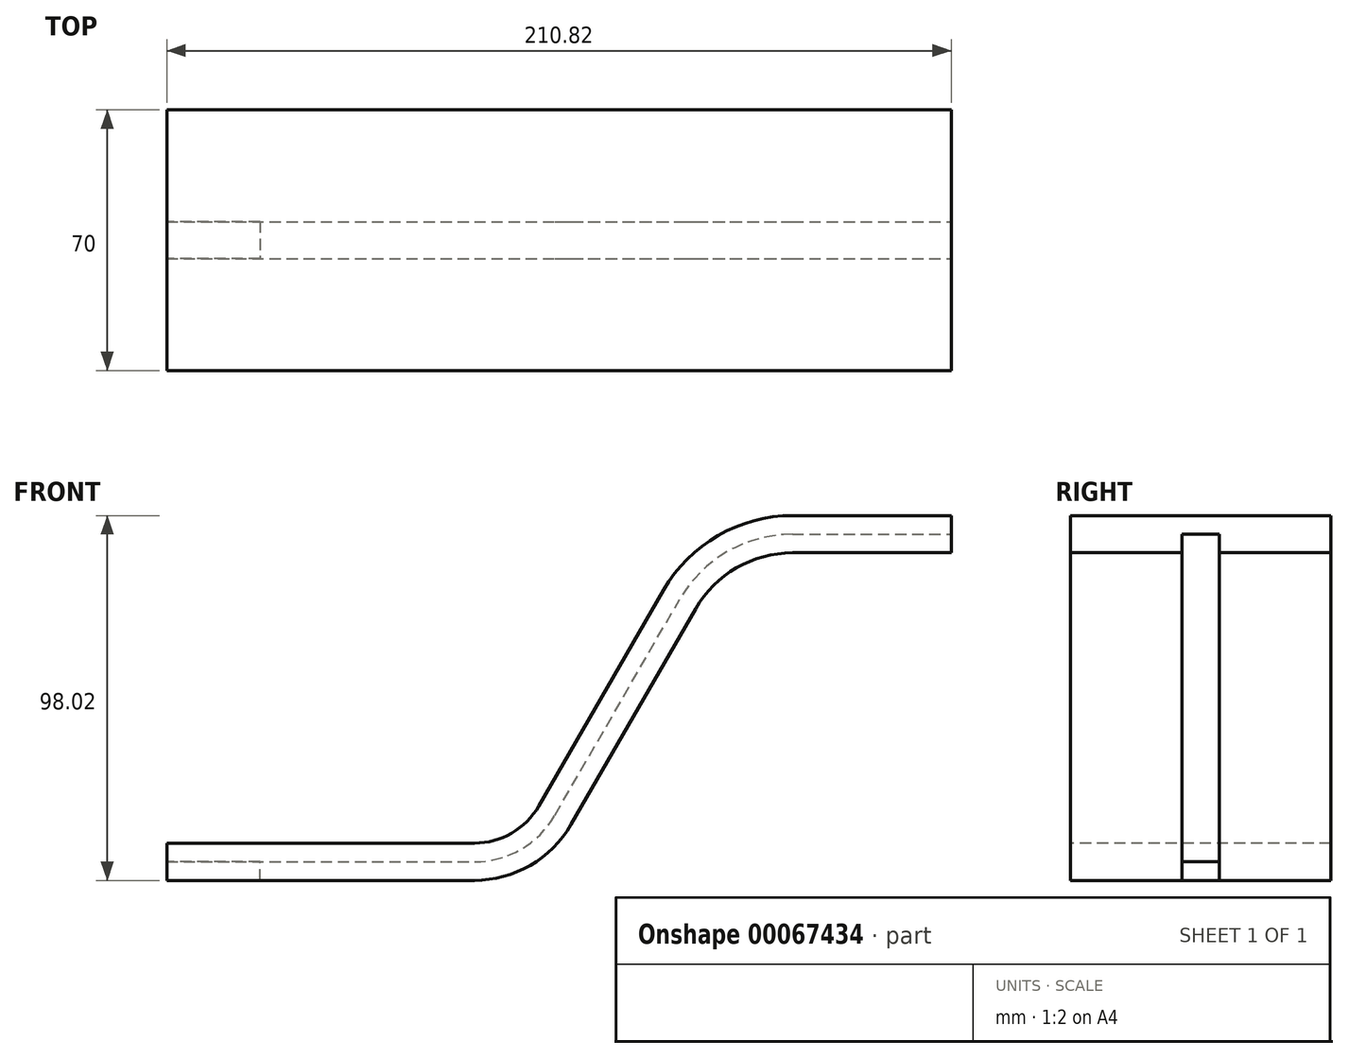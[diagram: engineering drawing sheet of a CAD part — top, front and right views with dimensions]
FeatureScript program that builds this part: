
annotation { "Feature Type Name" : "Feature", "Feature Type Description" : "" }
export const myFeature = defineFeature(function(context is Context, id is Id, definition is map)
    precondition{}
    {
        {
            var Q0;
            Q0=qCreatedBy(makeId("Front.planeOp"),FACE);
            var sketch = newSketch(context, id + "F0", { "sketchPlane" : qUnion([Q0])});
            skLineSegment(sketch, "E0", {"start": v(0, 0) * mm, "end": v(82.68, 0) * mm});
            skLineSegment(sketch, "E1", {"start": v(108.66, 15) * mm, "end": v(142.16, 73.02) * mm});
            skLineSegment(sketch, "E2", {"start": v(168.14, 88.02) * mm, "end": v(210.82, 88.02) * mm});
            skPoint(sketch, "E3.visualSharp", {"position": v(150.82, 88.02) * mm});
            skArc(sketch, "E3.filletArc", {"start": v(168.14, 88.02) * mm, "mid": v(153.14, 84) * mm, "end": v(142.16, 73.02) * mm});
            skPoint(sketch, "E4.visualSharp", {"position": v(100, 0) * mm});
            skArc(sketch, "E4.filletArc", {"start": v(82.68, 0) * mm, "mid": v(97.68, 4.02) * mm, "end": v(108.66, 15) * mm});
            skSolve(sketch);
        }
        {
            var Q0;
            Q0=qCreatedBy(makeId("Right.planeOp"),FACE);
            var sketch = newSketch(context, id + "F1", { "sketchPlane" : qUnion([Q0])});
            skLineSegment(sketch, "E5.bottom", {"start": v(35, 0) * mm, "end": v(5, 0) * mm});
            skLineSegment(sketch, "E5.top", {"start": v(35, 10) * mm, "end": v(-35, 10) * mm});
            skLineSegment(sketch, "E5.left", {"start": v(35, 0) * mm, "end": v(35, 10) * mm});
            skLineSegment(sketch, "E5.right", {"start": v(-35, 0) * mm, "end": v(-35, 10) * mm});
            skLineSegment(sketch, "E6.top", {"start": v(5, 5) * mm, "end": v(-5, 5) * mm});
            skLineSegment(sketch, "E6.left", {"start": v(5, 0) * mm, "end": v(5, 5) * mm});
            skLineSegment(sketch, "E6.right", {"start": v(-5, 0) * mm, "end": v(-5, 5) * mm});
            skLineSegment(sketch, "E7.trimOffspring", {"start": v(-5, 0) * mm, "end": v(-35, 0) * mm});
            skSolve(sketch);
        }
        {
            var Q0;
            Q0=makeQuery(id+"F1.imprint","IMPRINT",FACE,{"disambiguationData":[TD([[makeQuery(id+"F1.imprint","IMPRINT",EDGE,{"derivedFrom":sQuery(id+"F1.wireOp",EDGE,"E5.bottom")}),-1.0]])]});
            var Q1;
            Q1=sQuery(id+"F0.wireOp",EDGE,"E0");
            var Q2;
            Q2=sQuery(id+"F0.wireOp",EDGE,"E4.filletArc");
            var Q3;
            Q3=sQuery(id+"F0.wireOp",EDGE,"E1");
            var Q4;
            Q4=sQuery(id+"F0.wireOp",EDGE,"E3.filletArc");
            var Q5;
            Q5=sQuery(id+"F0.wireOp",EDGE,"E2");
            sweep(context, id + "F2", {"profiles" : qUnion([Q0]), "path" : qUnion([Q1, Q2, Q3, Q4, Q5])});
        }
        {
            var Q0;
            Q0=makeQuery(id+"F2.opSweep","CAP_FACE",FACE,{"disambiguationData":[OSD([sQuery(id+"F0.wireOp",VERTEX,"E0.start"),sQuery(id+"F1.wireOp",EDGE,"E5.bottom"),sQuery(id+"F1.wireOp",EDGE,"E5.top"),sQuery(id+"F1.wireOp",EDGE,"E5.left"),sQuery(id+"F1.wireOp",EDGE,"E5.right"),sQuery(id+"F1.wireOp",EDGE,"E6.top"),sQuery(id+"F1.wireOp",EDGE,"E6.left"),sQuery(id+"F1.wireOp",EDGE,"E6.right"),sQuery(id+"F1.wireOp",EDGE,"E7.trimOffspring")])],"isStart":true});
            var sketch = newSketch(context, id + "F3", { "sketchPlane" : qUnion([Q0])});
            skLineSegment(sketch, "E8", {"start": v(-5, 0) * mm, "end": v(5, 0) * mm});
            skLineSegment(sketch, "E9", {"start": v(5, 0) * mm, "end": v(5, 5) * mm});
            skLineSegment(sketch, "E10", {"start": v(5, 5) * mm, "end": v(-5, 5) * mm});
            skLineSegment(sketch, "E11", {"start": v(-5, 5) * mm, "end": v(-5, 0) * mm});
            skSolve(sketch);
        }
        {
            var Q0;
            Q0 = qSketchRegion(id + "F3", true);
            extrude(context, id + "F4", {"entities" : qUnion([Q0]), "oppositeDirection" : true, "depth" : 25 * mm});
        }
    });
